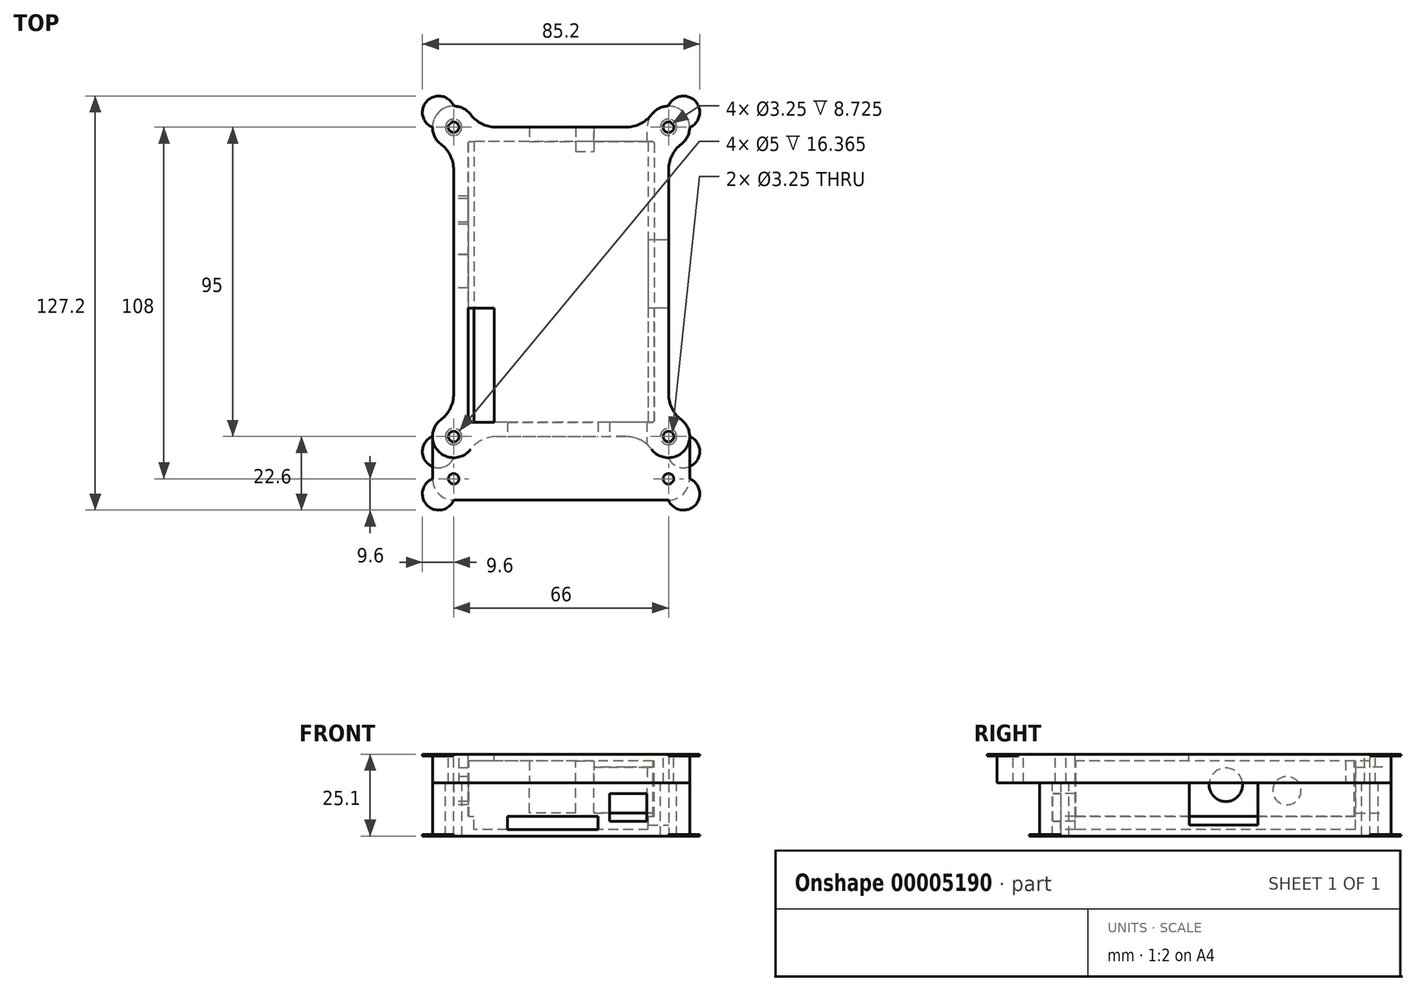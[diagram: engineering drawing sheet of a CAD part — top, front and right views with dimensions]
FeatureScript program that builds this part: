
annotation { "Feature Type Name" : "Feature", "Feature Type Description" : "" }
export const myFeature = defineFeature(function(context is Context, id is Id, definition is map)
    precondition{}
    {
        {
            var Q0;
            Q0=qCreatedBy(makeId("Top.planeOp"),FACE);
            var sketch = newSketch(context, id + "F0", { "sketchPlane" : qUnion([Q0])});
            skLineSegment(sketch, "E0.rect.bottom", {"start": v(28, 42.5) * mm, "end": v(-28, 42.5) * mm, "construction": true});
            skLineSegment(sketch, "E0.rect.top", {"start": v(28, -42.5) * mm, "end": v(-28, -42.5) * mm, "construction": true});
            skLineSegment(sketch, "E0.rect.left", {"start": v(28, 42.5) * mm, "end": v(28, -42.5) * mm, "construction": true});
            skLineSegment(sketch, "E0.rect.right", {"start": v(-28, 42.5) * mm, "end": v(-28, -42.5) * mm, "construction": true});
            skPoint(sketch, "E0.rect.middle", {"position": v(0, 0) * mm});
            skLineSegment(sketch, "E1.0", {"start": v(33, 47.5) * mm, "end": v(-33, 47.5) * mm});
            skLineSegment(sketch, "E1.1", {"start": v(33, 47.5) * mm, "end": v(33, -47.5) * mm});
            skLineSegment(sketch, "E1.2", {"start": v(33, -47.5) * mm, "end": v(-33, -47.5) * mm});
            skLineSegment(sketch, "E1.3", {"start": v(-33, 47.5) * mm, "end": v(-33, -47.5) * mm});
            skSolve(sketch);
        }
        {
            var Q0;
            Q0 = qSketchRegion(id + "F0", true);
            extrude(context, id + "F1", {"entities" : qUnion([Q0]), "depth" : (2 + 1.6 + 15.5 + 4) * mm});
        }
        {
            var Q0;
            Q0=makeQuery(id+"F1.opExtrude","CAP_FACE",FACE,{"disambiguationData":[OSD([sQuery(id+"F0.wireOp",EDGE,"E1.0"),sQuery(id+"F0.wireOp",EDGE,"E1.1"),sQuery(id+"F0.wireOp",EDGE,"E1.2"),sQuery(id+"F0.wireOp",EDGE,"E1.3")])],"isStart":false});
            var sketch = newSketch(context, id + "F2", { "sketchPlane" : qUnion([Q0])});
            skLineSegment(sketch, "E2.rect.bottom", {"start": v(28, 42.5) * mm, "end": v(-28, 42.5) * mm});
            skLineSegment(sketch, "E2.rect.top", {"start": v(28, -42.5) * mm, "end": v(-28, -42.5) * mm});
            skLineSegment(sketch, "E2.rect.left", {"start": v(28, 42.5) * mm, "end": v(28, -42.5) * mm});
            skLineSegment(sketch, "E2.rect.right", {"start": v(-28, 42.5) * mm, "end": v(-28, -42.5) * mm});
            skPoint(sketch, "E2.rect.middle", {"position": v(0, 0) * mm});
            skSolve(sketch);
        }
        {
            var Q0;
            Q0 = qSketchRegion(id + "F2", true);
            extrude(context, id + "F3", {"entities" : qUnion([Q0]), "operationType" : NewBodyOperationType.REMOVE, "oppositeDirection" : true, "depth" : (15.5 + 1.6) * mm});
        }
        {
            var Q0;
            Q0=makeQuery(id+"F3.boolean.opBoolean","COPY",FACE,{"derivedFrom":makeQuery(id+"F3.opExtrude","CAP_FACE",FACE,{"disambiguationData":[OSD([sQuery(id+"F2.wireOp",EDGE,"E2.rect.bottom"),sQuery(id+"F2.wireOp",EDGE,"E2.rect.top"),sQuery(id+"F2.wireOp",EDGE,"E2.rect.left"),sQuery(id+"F2.wireOp",EDGE,"E2.rect.right")])],"isStart":false})});
            var sketch = newSketch(context, id + "F4", { "sketchPlane" : qUnion([Q0])});
            skLineSegment(sketch, "E3.rect.bottom", {"start": v(26.75, 42.5) * mm, "end": v(-26.75, 42.5) * mm});
            skLineSegment(sketch, "E3.rect.top", {"start": v(26.75, -42.5) * mm, "end": v(-26.75, -42.5) * mm});
            skLineSegment(sketch, "E3.rect.left", {"start": v(26.75, 42.5) * mm, "end": v(26.75, -42.5) * mm});
            skLineSegment(sketch, "E3.rect.right", {"start": v(-26.75, 42.5) * mm, "end": v(-26.75, -42.5) * mm});
            skPoint(sketch, "E3.rect.middle", {"position": v(0, 0) * mm});
            skSolve(sketch);
        }
        {
            var Q0;
            Q0 = qSketchRegion(id + "F4", true);
            extrude(context, id + "F5", {"entities" : qUnion([Q0]), "operationType" : NewBodyOperationType.REMOVE, "oppositeDirection" : true, "depth" : 4 * mm});
        }
        {
            var Q0;
            Q0=makeQuery(id+"F1.opExtrude","SWEPT_FACE",FACE,{"disambiguationData":[OSD([sQuery(id+"F0.wireOp",EDGE,"E1.2")])]});
            var sketch = newSketch(context, id + "F6", { "sketchPlane" : qUnion([Q0])});
            skLineSegment(sketch, "E4.0", {"start": v(26.75, 2) * mm, "end": v(-26.75, 2) * mm, "construction": true});
            skLineSegment(sketch, "E4.1", {"start": v(-26.75, 6) * mm, "end": v(-28, 6) * mm, "construction": true});
            skLineSegment(sketch, "E5.bottom", {"start": v(-16.5, 2) * mm, "end": v(11.3, 2) * mm});
            skLineSegment(sketch, "E5.top", {"start": v(-16.5, 6) * mm, "end": v(11.3, 6) * mm});
            skLineSegment(sketch, "E5.left", {"start": v(-16.5, 2) * mm, "end": v(-16.5, 6) * mm});
            skLineSegment(sketch, "E5.right", {"start": v(11.3, 2) * mm, "end": v(11.3, 6) * mm});
            skLineSegment(sketch, "E6.0", {"start": v(28, 6) * mm, "end": v(26.75, 6) * mm, "construction": true});
            skLineSegment(sketch, "E7.bottom", {"start": v(24.4, 7.6) * mm, "end": v(16.8, 7.6) * mm, "construction": true});
            skLineSegment(sketch, "E7.top", {"start": v(24.4, 10) * mm, "end": v(16.8, 10) * mm, "construction": true});
            skLineSegment(sketch, "E7.left", {"start": v(24.4, 7.6) * mm, "end": v(24.4, 10) * mm, "construction": true});
            skLineSegment(sketch, "E7.right", {"start": v(16.8, 7.6) * mm, "end": v(16.8, 10) * mm, "construction": true});
            skLineSegment(sketch, "E8", {"start": v(20.6, 10) * mm, "end": v(20.6, 7.6) * mm, "construction": true});
            skPoint(sketch, "E9", {"position": v(20.6, 8.8) * mm});
            skLineSegment(sketch, "E10.rect.bottom", {"start": v(26.35, 13.05) * mm, "end": v(14.85, 13.05) * mm});
            skLineSegment(sketch, "E10.rect.top", {"start": v(26.35, 4.55) * mm, "end": v(14.85, 4.55) * mm});
            skLineSegment(sketch, "E10.rect.left", {"start": v(26.35, 13.05) * mm, "end": v(26.35, 4.55) * mm});
            skLineSegment(sketch, "E10.rect.right", {"start": v(14.85, 13.05) * mm, "end": v(14.85, 4.55) * mm});
            skSolve(sketch);
        }
        {
            var Q0;
            Q0 = qSketchRegion(id + "F6", true);
            var Q1;
            Q1=makeQuery(id+"F5.boolean.opBoolean","MERGE",FACE,{"derivedFrom":[makeQuery(id+"F3.boolean.opBoolean","COPY",FACE,{"derivedFrom":makeQuery(id+"F3.opExtrude","SWEPT_FACE",FACE,{"disambiguationData":[OSD([sQuery(id+"F2.wireOp",EDGE,"E2.rect.top")])]})}),makeQuery(id+"F5.opExtrude","SWEPT_FACE",FACE,{"disambiguationData":[OSD([sQuery(id+"F4.wireOp",EDGE,"E3.rect.top")])]})]});
            extrude(context, id + "F7", {"entities" : qUnion([Q0]), "operationType" : NewBodyOperationType.REMOVE, "endBound" : BoundingType.UP_TO_SURFACE, "oppositeDirection" : true, "endBoundEntityFace" : qUnion([Q1]), "depth" : 25 * mm});
        }
        {
            var Q0;
            Q0=makeQuery(id+"F1.opExtrude","SWEPT_FACE",FACE,{"disambiguationData":[OSD([sQuery(id+"F0.wireOp",EDGE,"E1.0")])]});
            var sketch = newSketch(context, id + "F8", { "sketchPlane" : qUnion([Q0])});
            skLineSegment(sketch, "E11.0", {"start": v(-28, 6) * mm, "end": v(-26.75, 6) * mm, "construction": true});
            skLineSegment(sketch, "E11.1", {"start": v(-26.75, 2) * mm, "end": v(26.75, 2) * mm, "construction": true});
            skLineSegment(sketch, "E11.2", {"start": v(26.75, 6) * mm, "end": v(28, 6) * mm, "construction": true});
            skLineSegment(sketch, "E12.bottom", {"start": v(-26, 7.6) * mm, "end": v(-10.6, 7.6) * mm, "construction": true});
            skLineSegment(sketch, "E12.top", {"start": v(-26, 20.6) * mm, "end": v(-10.6, 20.6) * mm, "construction": true});
            skLineSegment(sketch, "E12.left", {"start": v(-26, 7.6) * mm, "end": v(-26, 20.6) * mm, "construction": true});
            skLineSegment(sketch, "E12.right", {"start": v(-10.6, 7.6) * mm, "end": v(-10.6, 20.6) * mm, "construction": true});
            skLineSegment(sketch, "E13.bottom", {"start": v(-4.05, 7.6) * mm, "end": v(9.2, 7.6) * mm, "construction": true});
            skLineSegment(sketch, "E13.top", {"start": v(-4.05, 23.1) * mm, "end": v(9.2, 23.1) * mm, "construction": true});
            skLineSegment(sketch, "E13.left", {"start": v(-4.05, 7.6) * mm, "end": v(-4.05, 23.1) * mm, "construction": true});
            skLineSegment(sketch, "E13.right", {"start": v(9.2, 7.6) * mm, "end": v(9.2, 23.1) * mm, "construction": true});
            skLineSegment(sketch, "E14.0", {"start": v(-26.5, 21.1) * mm, "end": v(-10.1, 21.1) * mm});
            skLineSegment(sketch, "E14.1", {"start": v(-26.5, 7.1) * mm, "end": v(-26.5, 21.1) * mm});
            skLineSegment(sketch, "E14.2", {"start": v(-26.5, 7.1) * mm, "end": v(-10.1, 7.1) * mm});
            skLineSegment(sketch, "E14.3", {"start": v(-10.1, 7.1) * mm, "end": v(-10.1, 21.1) * mm});
            skLineSegment(sketch, "E15.0", {"start": v(-4.55, 23.6) * mm, "end": v(9.7, 23.6) * mm});
            skLineSegment(sketch, "E15.1", {"start": v(-4.55, 7.1) * mm, "end": v(-4.55, 23.6) * mm});
            skLineSegment(sketch, "E15.2", {"start": v(-4.55, 7.1) * mm, "end": v(9.7, 7.1) * mm});
            skLineSegment(sketch, "E15.3", {"start": v(9.7, 7.1) * mm, "end": v(9.7, 23.6) * mm});
            skSolve(sketch);
        }
        {
            var Q0;
            Q0 = qSketchRegion(id + "F8", true);
            var Q1;
            Q1=makeQuery(id+"F5.boolean.opBoolean","MERGE",FACE,{"derivedFrom":[makeQuery(id+"F3.boolean.opBoolean","COPY",FACE,{"derivedFrom":makeQuery(id+"F3.opExtrude","SWEPT_FACE",FACE,{"disambiguationData":[OSD([sQuery(id+"F2.wireOp",EDGE,"E2.rect.bottom")])]})}),makeQuery(id+"F5.opExtrude","SWEPT_FACE",FACE,{"disambiguationData":[OSD([sQuery(id+"F4.wireOp",EDGE,"E3.rect.bottom")])]})]});
            extrude(context, id + "F9", {"entities" : qUnion([Q0]), "operationType" : NewBodyOperationType.REMOVE, "endBound" : BoundingType.UP_TO_SURFACE, "oppositeDirection" : true, "endBoundEntityFace" : qUnion([Q1]), "depth" : 25 * mm});
        }
        {
            var Q0;
            Q0=makeQuery(id+"F1.opExtrude","SWEPT_FACE",FACE,{"disambiguationData":[OSD([sQuery(id+"F0.wireOp",EDGE,"E1.1")])]});
            var sketch = newSketch(context, id + "F10", { "sketchPlane" : qUnion([Q0])});
            skLineSegment(sketch, "E16.0", {"start": v(42.5, 6) * mm, "end": v(-42.5, 6) * mm, "construction": true});
            skLineSegment(sketch, "E17.bottom", {"start": v(-5, 6.8) * mm, "end": v(10.1, 6.8) * mm, "construction": true});
            skLineSegment(sketch, "E17.top", {"start": v(-5, 12.95) * mm, "end": v(10.1, 12.95) * mm, "construction": true});
            skLineSegment(sketch, "E17.left", {"start": v(-5, 6.8) * mm, "end": v(-5, 12.95) * mm, "construction": true});
            skLineSegment(sketch, "E17.right", {"start": v(10.1, 6.8) * mm, "end": v(10.1, 12.95) * mm, "construction": true});
            skLineSegment(sketch, "E18", {"start": v(2.55, 12.95) * mm, "end": v(2.55, 6.8) * mm, "construction": true});
            skPoint(sketch, "E19", {"position": v(2.55, 9.88) * mm});
            skLineSegment(sketch, "E20.rect.bottom", {"start": v(13.05, 16.38) * mm, "end": v(-7.95, 16.38) * mm});
            skLineSegment(sketch, "E20.rect.top", {"start": v(13.05, 3.38) * mm, "end": v(-7.95, 3.38) * mm});
            skLineSegment(sketch, "E20.rect.left", {"start": v(13.05, 16.38) * mm, "end": v(13.05, 3.38) * mm});
            skLineSegment(sketch, "E20.rect.right", {"start": v(-7.95, 16.38) * mm, "end": v(-7.95, 3.38) * mm});
            skSolve(sketch);
        }
        {
            var Q0;
            Q0 = qSketchRegion(id + "F10", true);
            var Q1;
            Q1=makeQuery(id+"F5.boolean.opBoolean","COPY",FACE,{"derivedFrom":makeQuery(id+"F5.opExtrude","SWEPT_FACE",FACE,{"disambiguationData":[OSD([sQuery(id+"F4.wireOp",EDGE,"E3.rect.left")])]})});
            extrude(context, id + "F11", {"entities" : qUnion([Q0]), "operationType" : NewBodyOperationType.REMOVE, "endBound" : BoundingType.UP_TO_SURFACE, "oppositeDirection" : true, "endBoundEntityFace" : qUnion([Q1]), "depth" : 25 * mm});
        }
        {
            var Q0;
            Q0=makeQuery(id+"F1.opExtrude","SWEPT_FACE",FACE,{"disambiguationData":[OSD([sQuery(id+"F0.wireOp",EDGE,"E1.3")])]});
            var sketch = newSketch(context, id + "F12", { "sketchPlane" : qUnion([Q0])});
            skLineSegment(sketch, "E21.0", {"start": v(-42.5, 6) * mm, "end": v(42.5, 6) * mm, "construction": true});
            skCircle(sketch, "E22", {"center": v(-22, 13.95) * mm, "radius": 3.35 * mm, "construction": true});
            skCircle(sketch, "E23", {"center": v(-3.25, 15.75) * mm, "radius": 4.15 * mm, "construction": true});
            skPoint(sketch, "E24", {"position": v(-22, 10.6) * mm});
            skPoint(sketch, "E25", {"position": v(-3.25, 11.6) * mm});
            skCircle(sketch, "E26.0", {"center": v(-22, 13.95) * mm, "radius": 4.35 * mm});
            skCircle(sketch, "E27.0", {"center": v(-3.25, 15.75) * mm, "radius": 5.15 * mm});
            skSolve(sketch);
        }
        {
            var Q0;
            Q0 = qSketchRegion(id + "F12", true);
            var Q1;
            Q1=makeQuery(id+"F3.boolean.opBoolean","COPY",FACE,{"derivedFrom":makeQuery(id+"F3.opExtrude","SWEPT_FACE",FACE,{"disambiguationData":[OSD([sQuery(id+"F2.wireOp",EDGE,"E2.rect.right")])]})});
            extrude(context, id + "F13", {"entities" : qUnion([Q0]), "operationType" : NewBodyOperationType.REMOVE, "endBound" : BoundingType.UP_TO_SURFACE, "oppositeDirection" : true, "endBoundEntityFace" : qUnion([Q1]), "depth" : 25 * mm});
        }
        {
            var Q0;
            Q0=makeQuery(id+"F1.opExtrude","CAP_FACE",FACE,{"disambiguationData":[OSD([sQuery(id+"F0.wireOp",EDGE,"E1.0"),sQuery(id+"F0.wireOp",EDGE,"E1.1"),sQuery(id+"F0.wireOp",EDGE,"E1.2"),sQuery(id+"F0.wireOp",EDGE,"E1.3")])],"isStart":false});
            var sketch = newSketch(context, id + "F14", { "sketchPlane" : qUnion([Q0])});
            skLineSegment(sketch, "E28.rect.bottom", {"start": v(28.58, 43.08) * mm, "end": v(-28.57, 43.08) * mm});
            skLineSegment(sketch, "E28.rect.top", {"start": v(28.57, -43.07) * mm, "end": v(-28.58, -43.07) * mm});
            skLineSegment(sketch, "E28.rect.left", {"start": v(28.58, 43.08) * mm, "end": v(28.57, -43.07) * mm});
            skLineSegment(sketch, "E28.rect.right", {"start": v(-28.57, 43.08) * mm, "end": v(-28.58, -43.07) * mm});
            skPoint(sketch, "E28.rect.middle", {"position": v(0, 0) * mm});
            skSolve(sketch);
        }
        {
            var Q0;
            Q0 = qSketchRegion(id + "F14", true);
            var Q1;
            {var subQ0=sQuery(id+"F2.wireOp",EDGE,"E2.rect.bottom");var subQ1=sQuery(id+"F2.wireOp",EDGE,"E2.rect.top");var subQ2=sQuery(id+"F2.wireOp",EDGE,"E2.rect.right");Q1=makeQuery(id+"F5.boolean.opBoolean","SPLIT",FACE,{"disambiguationData":[TD([makeQuery(id+"F3.boolean.opBoolean","COPY",FACE,{"derivedFrom":makeQuery(id+"F3.opExtrude","SWEPT_FACE",FACE,{"disambiguationData":[OSD([subQ2])]})})])],"derivedFrom":makeQuery(id+"F3.boolean.opBoolean","COPY",FACE,{"derivedFrom":makeQuery(id+"F3.opExtrude","CAP_FACE",FACE,{"disambiguationData":[OSD([subQ0,subQ1,sQuery(id+"F2.wireOp",EDGE,"E2.rect.left"),subQ2])],"isStart":false})})});}
            extrude(context, id + "F15", {"entities" : qUnion([Q0]), "operationType" : NewBodyOperationType.REMOVE, "endBound" : BoundingType.UP_TO_SURFACE, "oppositeDirection" : true, "endBoundEntityFace" : qUnion([Q1]), "depth" : 25 * mm});
        }
        {
            var Q0;
            {var subQ0=sQuery(id+"F2.wireOp",EDGE,"E2.rect.bottom");var subQ1=sQuery(id+"F2.wireOp",EDGE,"E2.rect.top");var subQ2=sQuery(id+"F2.wireOp",EDGE,"E2.rect.left");var subQ3=sQuery(id+"F2.wireOp",EDGE,"E2.rect.right");var subQ4=makeQuery(id+"F3.boolean.opBoolean","COPY",FACE,{"derivedFrom":makeQuery(id+"F3.opExtrude","CAP_FACE",FACE,{"disambiguationData":[OSD([subQ0,subQ1,subQ2,subQ3])],"isStart":false})});var subQ8=makeQuery(id+"F3.boolean.opBoolean","COPY",FACE,{"derivedFrom":makeQuery(id+"F3.opExtrude","SWEPT_FACE",FACE,{"disambiguationData":[OSD([subQ0])]})});var subQ10=makeQuery(id+"F3.boolean.opBoolean","COPY",FACE,{"derivedFrom":makeQuery(id+"F3.opExtrude","SWEPT_FACE",FACE,{"disambiguationData":[OSD([subQ2])]})});Q0=makeQuery(id+"F15.boolean.opBoolean","MERGE",FACE,{"derivedFrom":[makeQuery(id+"F5.boolean.opBoolean","SPLIT",FACE,{"disambiguationData":[TD([makeQuery(id+"F3.boolean.opBoolean","COPY",FACE,{"derivedFrom":makeQuery(id+"F3.opExtrude","SWEPT_FACE",FACE,{"disambiguationData":[OSD([subQ3])]})})])],"derivedFrom":subQ4}),makeQuery(id+"F11.boolean.opBoolean","SPLIT",FACE,{"disambiguationData":[TD([subQ8])],"derivedFrom":makeQuery(id+"F5.boolean.opBoolean","SPLIT",FACE,{"disambiguationData":[TD([subQ10])],"derivedFrom":subQ4})}),makeQuery(id+"F15.opExtrude","CAP_FACE",FACE,{"disambiguationData":[OSD([sQuery(id+"F14.wireOp",EDGE,"E28.rect.bottom"),sQuery(id+"F14.wireOp",EDGE,"E28.rect.top"),sQuery(id+"F14.wireOp",EDGE,"E28.rect.left"),sQuery(id+"F14.wireOp",EDGE,"E28.rect.right")])],"isStart":false})]});}
            var sketch = newSketch(context, id + "F16", { "sketchPlane" : qUnion([Q0])});
            skLineSegment(sketch, "E29.bottom", {"start": v(-26.75, 42.5) * mm, "end": v(26.75, 42.5) * mm});
            skLineSegment(sketch, "E29.top", {"start": v(-26.75, 43.08) * mm, "end": v(26.75, 43.08) * mm});
            skLineSegment(sketch, "E29.left", {"start": v(-26.75, 42.5) * mm, "end": v(-26.75, 43.08) * mm});
            skLineSegment(sketch, "E29.right", {"start": v(26.75, 42.5) * mm, "end": v(26.75, 43.08) * mm});
            skLineSegment(sketch, "E30.bottom", {"start": v(-26.75, -42.5) * mm, "end": v(26.75, -42.5) * mm});
            skLineSegment(sketch, "E30.top", {"start": v(-26.75, -43.07) * mm, "end": v(26.75, -43.07) * mm});
            skLineSegment(sketch, "E30.left", {"start": v(-26.75, -42.5) * mm, "end": v(-26.75, -43.07) * mm});
            skLineSegment(sketch, "E30.right", {"start": v(26.75, -42.5) * mm, "end": v(26.75, -43.07) * mm});
            skSolve(sketch);
        }
        {
            var Q0;
            Q0 = qSketchRegion(id + "F16", true);
            var Q1;
            Q1=makeQuery(id+"F7.boolean.opBoolean","MERGE",FACE,{"derivedFrom":[makeQuery(id+"F5.boolean.opBoolean","COPY",FACE,{"derivedFrom":makeQuery(id+"F5.opExtrude","CAP_FACE",FACE,{"disambiguationData":[OSD([sQuery(id+"F4.wireOp",EDGE,"E3.rect.bottom"),sQuery(id+"F4.wireOp",EDGE,"E3.rect.top"),sQuery(id+"F4.wireOp",EDGE,"E3.rect.left"),sQuery(id+"F4.wireOp",EDGE,"E3.rect.right")])],"isStart":false})}),makeQuery(id+"F7.opExtrude","SWEPT_FACE",FACE,{"disambiguationData":[OSD([sQuery(id+"F6.wireOp",EDGE,"E5.bottom")])]})]});
            extrude(context, id + "F17", {"entities" : qUnion([Q0]), "operationType" : NewBodyOperationType.REMOVE, "endBound" : BoundingType.UP_TO_SURFACE, "oppositeDirection" : true, "endBoundEntityFace" : qUnion([Q1]), "depth" : 25 * mm});
        }
        {
            var Q0;
            Q0=makeQuery(id+"F1.opExtrude","CAP_FACE",FACE,{"disambiguationData":[OSD([sQuery(id+"F0.wireOp",EDGE,"E1.0"),sQuery(id+"F0.wireOp",EDGE,"E1.1"),sQuery(id+"F0.wireOp",EDGE,"E1.2"),sQuery(id+"F0.wireOp",EDGE,"E1.3")])],"isStart":false});
            var sketch = newSketch(context, id + "F18", { "sketchPlane" : qUnion([Q0])});
            skLineSegment(sketch, "E31.bottom", {"start": v(-33, 47.5) * mm, "end": v(33, 47.5) * mm});
            skLineSegment(sketch, "E31.top", {"start": v(-33, -47.5) * mm, "end": v(33, -47.5) * mm});
            skLineSegment(sketch, "E31.left", {"start": v(-33, 47.5) * mm, "end": v(-33, -47.5) * mm});
            skLineSegment(sketch, "E31.right", {"start": v(33, 47.5) * mm, "end": v(33, -47.5) * mm});
            skSolve(sketch);
        }
        {
            var Q0;
            Q0 = qSketchRegion(id + "F18", true);
            extrude(context, id + "F19", {"entities" : qUnion([Q0]), "operationType" : NewBodyOperationType.ADD, "depth" : 2 * mm});
        }
        {
            var Q0;
            Q0=makeQuery(id+"F19.opExtrude","CAP_FACE",FACE,{"disambiguationData":[OSD([sQuery(id+"F18.wireOp",EDGE,"E31.bottom"),sQuery(id+"F18.wireOp",EDGE,"E31.top"),sQuery(id+"F18.wireOp",EDGE,"E31.left"),sQuery(id+"F18.wireOp",EDGE,"E31.right")])],"isStart":false});
            var sketch = newSketch(context, id + "F20", { "sketchPlane" : qUnion([Q0])});
            skCircle(sketch, "E32", {"center": v(-33, 47.5) * mm, "radius": 6.5 * mm});
            skCircle(sketch, "E33", {"center": v(33, 47.5) * mm, "radius": 6.5 * mm});
            skCircle(sketch, "E34", {"center": v(33, -47.5) * mm, "radius": 6.5 * mm});
            skCircle(sketch, "E35", {"center": v(-33, -47.5) * mm, "radius": 6.5 * mm});
            skSolve(sketch);
        }
        {
            var Q0;
            Q0 = qSketchRegion(id + "F20", true);
            var Q1;
            Q1=makeQuery(id+"F1.opExtrude","CAP_FACE",FACE,{"disambiguationData":[OSD([sQuery(id+"F0.wireOp",EDGE,"E1.0"),sQuery(id+"F0.wireOp",EDGE,"E1.1"),sQuery(id+"F0.wireOp",EDGE,"E1.2"),sQuery(id+"F0.wireOp",EDGE,"E1.3")])],"isStart":true});
            extrude(context, id + "F21", {"entities" : qUnion([Q0]), "operationType" : NewBodyOperationType.ADD, "endBound" : BoundingType.UP_TO_SURFACE, "oppositeDirection" : true, "endBoundEntityFace" : qUnion([Q1]), "depth" : 25 * mm});
        }
        {
            var Q0;
            Q0=makeQuery(id+"F21.boolean.opBoolean","MERGE",FACE,{"derivedFrom":[makeQuery(id+"F19.opExtrude","CAP_FACE",FACE,{"disambiguationData":[OSD([sQuery(id+"F18.wireOp",EDGE,"E31.bottom"),sQuery(id+"F18.wireOp",EDGE,"E31.top"),sQuery(id+"F18.wireOp",EDGE,"E31.left"),sQuery(id+"F18.wireOp",EDGE,"E31.right")])],"isStart":false}),makeQuery(id+"F21.opExtrude","CAP_FACE",FACE,{"disambiguationData":[OSD([sQuery(id+"F20.wireOp",EDGE,"E32")])],"isStart":true}),makeQuery(id+"F21.opExtrude","CAP_FACE",FACE,{"disambiguationData":[OSD([sQuery(id+"F20.wireOp",EDGE,"E33")])],"isStart":true}),makeQuery(id+"F21.opExtrude","CAP_FACE",FACE,{"disambiguationData":[OSD([sQuery(id+"F20.wireOp",EDGE,"E34")])],"isStart":true}),makeQuery(id+"F21.opExtrude","CAP_FACE",FACE,{"disambiguationData":[OSD([sQuery(id+"F20.wireOp",EDGE,"E35")])],"isStart":true})]});
            var sketch = newSketch(context, id + "F22", { "sketchPlane" : qUnion([Q0])});
            skCircle(sketch, "E36", {"center": v(-33, -47.5) * mm, "radius": 1.63 * mm});
            skCircle(sketch, "E37", {"center": v(33, -47.5) * mm, "radius": 1.63 * mm});
            skCircle(sketch, "E38", {"center": v(33, 47.5) * mm, "radius": 1.63 * mm});
            skCircle(sketch, "E39", {"center": v(-33, 47.5) * mm, "radius": 1.63 * mm});
            skSolve(sketch);
        }
        {
            var Q0;
            Q0 = qSketchRegion(id + "F22", true);
            extrude(context, id + "F23", {"entities" : qUnion([Q0]), "operationType" : NewBodyOperationType.REMOVE, "endBound" : BoundingType.THROUGH_ALL, "oppositeDirection" : true, "depth" : 25 * mm});
        }
        {
            var Q0;
            Q0=makeQuery(id+"F21.boolean.opBoolean","INTERSECT",EDGE,{"derivedFrom":[makeQuery(id+"F19.boolean.opBoolean","MERGE",FACE,{"derivedFrom":[makeQuery(id+"F1.opExtrude","SWEPT_FACE",FACE,{"disambiguationData":[OSD([sQuery(id+"F0.wireOp",EDGE,"E1.3")])]}),makeQuery(id+"F19.opExtrude","SWEPT_FACE",FACE,{"disambiguationData":[OSD([sQuery(id+"F18.wireOp",EDGE,"E31.left")])]})]}),makeQuery(id+"F21.opExtrude","SWEPT_FACE",FACE,{"disambiguationData":[OSD([sQuery(id+"F20.wireOp",EDGE,"E32")])]})]});
            var Q1;
            Q1=makeQuery(id+"F21.boolean.opBoolean","INTERSECT",EDGE,{"derivedFrom":[makeQuery(id+"F19.boolean.opBoolean","MERGE",FACE,{"derivedFrom":[makeQuery(id+"F1.opExtrude","SWEPT_FACE",FACE,{"disambiguationData":[OSD([sQuery(id+"F0.wireOp",EDGE,"E1.3")])]}),makeQuery(id+"F19.opExtrude","SWEPT_FACE",FACE,{"disambiguationData":[OSD([sQuery(id+"F18.wireOp",EDGE,"E31.left")])]})]}),makeQuery(id+"F21.opExtrude","SWEPT_FACE",FACE,{"disambiguationData":[OSD([sQuery(id+"F20.wireOp",EDGE,"E35")])]})]});
            var Q2;
            Q2=makeQuery(id+"F21.boolean.opBoolean","INTERSECT",EDGE,{"derivedFrom":[makeQuery(id+"F19.boolean.opBoolean","MERGE",FACE,{"derivedFrom":[makeQuery(id+"F1.opExtrude","SWEPT_FACE",FACE,{"disambiguationData":[OSD([sQuery(id+"F0.wireOp",EDGE,"E1.2")])]}),makeQuery(id+"F19.opExtrude","SWEPT_FACE",FACE,{"disambiguationData":[OSD([sQuery(id+"F18.wireOp",EDGE,"E31.top")])]})]}),makeQuery(id+"F21.opExtrude","SWEPT_FACE",FACE,{"disambiguationData":[OSD([sQuery(id+"F20.wireOp",EDGE,"E35")])]})]});
            var Q3;
            Q3=makeQuery(id+"F21.boolean.opBoolean","INTERSECT",EDGE,{"derivedFrom":[makeQuery(id+"F19.boolean.opBoolean","MERGE",FACE,{"derivedFrom":[makeQuery(id+"F1.opExtrude","SWEPT_FACE",FACE,{"disambiguationData":[OSD([sQuery(id+"F0.wireOp",EDGE,"E1.2")])]}),makeQuery(id+"F19.opExtrude","SWEPT_FACE",FACE,{"disambiguationData":[OSD([sQuery(id+"F18.wireOp",EDGE,"E31.top")])]})]}),makeQuery(id+"F21.opExtrude","SWEPT_FACE",FACE,{"disambiguationData":[OSD([sQuery(id+"F20.wireOp",EDGE,"E34")])]})]});
            var Q4;
            Q4=makeQuery(id+"F21.boolean.opBoolean","INTERSECT",EDGE,{"derivedFrom":[makeQuery(id+"F19.boolean.opBoolean","MERGE",FACE,{"derivedFrom":[makeQuery(id+"F1.opExtrude","SWEPT_FACE",FACE,{"disambiguationData":[OSD([sQuery(id+"F0.wireOp",EDGE,"E1.1")])]}),makeQuery(id+"F19.opExtrude","SWEPT_FACE",FACE,{"disambiguationData":[OSD([sQuery(id+"F18.wireOp",EDGE,"E31.right")])]})]}),makeQuery(id+"F21.opExtrude","SWEPT_FACE",FACE,{"disambiguationData":[OSD([sQuery(id+"F20.wireOp",EDGE,"E34")])]})]});
            var Q5;
            Q5=makeQuery(id+"F21.boolean.opBoolean","INTERSECT",EDGE,{"derivedFrom":[makeQuery(id+"F19.boolean.opBoolean","MERGE",FACE,{"derivedFrom":[makeQuery(id+"F1.opExtrude","SWEPT_FACE",FACE,{"disambiguationData":[OSD([sQuery(id+"F0.wireOp",EDGE,"E1.1")])]}),makeQuery(id+"F19.opExtrude","SWEPT_FACE",FACE,{"disambiguationData":[OSD([sQuery(id+"F18.wireOp",EDGE,"E31.right")])]})]}),makeQuery(id+"F21.opExtrude","SWEPT_FACE",FACE,{"disambiguationData":[OSD([sQuery(id+"F20.wireOp",EDGE,"E33")])]})]});
            var Q6;
            Q6=makeQuery(id+"F21.boolean.opBoolean","INTERSECT",EDGE,{"derivedFrom":[makeQuery(id+"F19.boolean.opBoolean","MERGE",FACE,{"derivedFrom":[makeQuery(id+"F1.opExtrude","SWEPT_FACE",FACE,{"disambiguationData":[OSD([sQuery(id+"F0.wireOp",EDGE,"E1.0")])]}),makeQuery(id+"F19.opExtrude","SWEPT_FACE",FACE,{"disambiguationData":[OSD([sQuery(id+"F18.wireOp",EDGE,"E31.bottom")])]})]}),makeQuery(id+"F21.opExtrude","SWEPT_FACE",FACE,{"disambiguationData":[OSD([sQuery(id+"F20.wireOp",EDGE,"E33")])]})]});
            var Q7;
            Q7=makeQuery(id+"F21.boolean.opBoolean","INTERSECT",EDGE,{"derivedFrom":[makeQuery(id+"F19.boolean.opBoolean","MERGE",FACE,{"derivedFrom":[makeQuery(id+"F1.opExtrude","SWEPT_FACE",FACE,{"disambiguationData":[OSD([sQuery(id+"F0.wireOp",EDGE,"E1.0")])]}),makeQuery(id+"F19.opExtrude","SWEPT_FACE",FACE,{"disambiguationData":[OSD([sQuery(id+"F18.wireOp",EDGE,"E31.bottom")])]})]}),makeQuery(id+"F21.opExtrude","SWEPT_FACE",FACE,{"disambiguationData":[OSD([sQuery(id+"F20.wireOp",EDGE,"E32")])]})]});
            fillet(context, id + "F24", {"entities" : qUnion([Q0, Q1, Q2, Q3, Q4, Q5, Q6, Q7]), "radius" : 10 * mm, "tangentPropagation" : true, "allowEdgeOverflow" : false});
        }
        {
            var Q0;
            Q0=makeQuery(id+"F19.boolean.opBoolean","MERGE",FACE,{"derivedFrom":[makeQuery(id+"F1.opExtrude","SWEPT_FACE",FACE,{"disambiguationData":[OSD([sQuery(id+"F0.wireOp",EDGE,"E1.1")])]}),makeQuery(id+"F19.opExtrude","SWEPT_FACE",FACE,{"disambiguationData":[OSD([sQuery(id+"F18.wireOp",EDGE,"E31.right")])]})]});
            var sketch = newSketch(context, id + "F25", { "sketchPlane" : qUnion([Q0])});
            skLineSegment(sketch, "E40.bottom", {"start": v(-61.72, 16.38) * mm, "end": v(58.28, 16.38) * mm});
            skLineSegment(sketch, "E40.top", {"start": v(-61.72, 16.37) * mm, "end": v(58.28, 16.37) * mm});
            skLineSegment(sketch, "E40.left", {"start": v(-61.72, 16.38) * mm, "end": v(-61.72, 16.37) * mm});
            skLineSegment(sketch, "E40.right", {"start": v(58.28, 16.38) * mm, "end": v(58.28, 16.37) * mm});
            skSolve(sketch);
        }
        {
            var Q0;
            Q0 = qSketchRegion(id + "F25", true);
            extrude(context, id + "F26", {"entities" : qUnion([Q0]), "operationType" : NewBodyOperationType.REMOVE, "endBound" : BoundingType.THROUGH_ALL, "oppositeDirection" : true, "depth" : 25 * mm, "hasSecondDirection" : true, "secondDirectionBound" : BoundingType.THROUGH_ALL, "secondDirectionOppositeDirection" : false, "secondDirectionDepth" : 25 * mm});
        }
        {
            var Q0;
            Q0=makeQuery(id+"F21.boolean.opBoolean","MERGE",FACE,{"derivedFrom":[makeQuery(id+"F19.opExtrude","CAP_FACE",FACE,{"disambiguationData":[OSD([sQuery(id+"F18.wireOp",EDGE,"E31.bottom"),sQuery(id+"F18.wireOp",EDGE,"E31.top"),sQuery(id+"F18.wireOp",EDGE,"E31.left"),sQuery(id+"F18.wireOp",EDGE,"E31.right")])],"isStart":false}),makeQuery(id+"F21.opExtrude","CAP_FACE",FACE,{"disambiguationData":[OSD([sQuery(id+"F20.wireOp",EDGE,"E32")])],"isStart":true}),makeQuery(id+"F21.opExtrude","CAP_FACE",FACE,{"disambiguationData":[OSD([sQuery(id+"F20.wireOp",EDGE,"E33")])],"isStart":true}),makeQuery(id+"F21.opExtrude","CAP_FACE",FACE,{"disambiguationData":[OSD([sQuery(id+"F20.wireOp",EDGE,"E34")])],"isStart":true}),makeQuery(id+"F21.opExtrude","CAP_FACE",FACE,{"disambiguationData":[OSD([sQuery(id+"F20.wireOp",EDGE,"E35")])],"isStart":true})]});
            var sketch = newSketch(context, id + "F27", { "sketchPlane" : qUnion([Q0])});
            skLineSegment(sketch, "E41.bottom", {"start": v(-28.58, -43.07) * mm, "end": v(-20.57, -43.07) * mm});
            skLineSegment(sketch, "E41.top", {"start": v(-28.58, -8.08) * mm, "end": v(-20.58, -8.08) * mm});
            skLineSegment(sketch, "E41.left", {"start": v(-28.57, -43.07) * mm, "end": v(-28.58, -8.07) * mm});
            skLineSegment(sketch, "E41.right", {"start": v(-20.57, -43.07) * mm, "end": v(-20.58, -8.07) * mm});
            skSolve(sketch);
        }
        {
            var Q0;
            Q0 = qSketchRegion(id + "F27", true);
            extrude(context, id + "F28", {"entities" : qUnion([Q0]), "operationType" : NewBodyOperationType.REMOVE, "endBound" : BoundingType.UP_TO_NEXT, "oppositeDirection" : true, "depth" : 3 * mm});
        }
        {
            var Q0;
            Q0=makeQuery(id+"F26.boolean.opBoolean","COPY",FACE,{"disambiguationData":[OD(1.0)],"derivedFrom":makeQuery(id+"F26.opExtrude","SWEPT_FACE",FACE,{"disambiguationData":[OSD([sQuery(id+"F25.wireOp",EDGE,"E40.top")])]})});
            var sketch = newSketch(context, id + "F29", { "sketchPlane" : qUnion([Q0])});
            skCircle(sketch, "E42", {"center": v(-33, 47.5) * mm, "radius": 2.5 * mm});
            skCircle(sketch, "E43", {"center": v(33, 47.5) * mm, "radius": 2.5 * mm});
            skCircle(sketch, "E44", {"center": v(-33, -47.5) * mm, "radius": 2.5 * mm});
            skCircle(sketch, "E45", {"center": v(33, -47.5) * mm, "radius": 2.5 * mm});
            skSolve(sketch);
        }
        {
            var Q0;
            Q0 = qSketchRegion(id + "F29", true);
            var Q1;
            Q1=makeQuery(id+"F17.boolean.opBoolean","MERGE",FACE,{"derivedFrom":[makeQuery(id+"F7.boolean.opBoolean","MERGE",FACE,{"derivedFrom":[makeQuery(id+"F5.boolean.opBoolean","COPY",FACE,{"derivedFrom":makeQuery(id+"F5.opExtrude","CAP_FACE",FACE,{"disambiguationData":[OSD([sQuery(id+"F4.wireOp",EDGE,"E3.rect.bottom"),sQuery(id+"F4.wireOp",EDGE,"E3.rect.top"),sQuery(id+"F4.wireOp",EDGE,"E3.rect.left"),sQuery(id+"F4.wireOp",EDGE,"E3.rect.right")])],"isStart":false})}),makeQuery(id+"F7.opExtrude","SWEPT_FACE",FACE,{"disambiguationData":[OSD([sQuery(id+"F6.wireOp",EDGE,"E5.bottom")])]})]}),makeQuery(id+"F17.opExtrude","CAP_FACE",FACE,{"disambiguationData":[OSD([sQuery(id+"F16.wireOp",EDGE,"E29.bottom"),sQuery(id+"F16.wireOp",EDGE,"E29.top"),sQuery(id+"F16.wireOp",EDGE,"E29.left"),sQuery(id+"F16.wireOp",EDGE,"E29.right")])],"isStart":false}),makeQuery(id+"F17.opExtrude","CAP_FACE",FACE,{"disambiguationData":[OSD([sQuery(id+"F16.wireOp",EDGE,"E30.bottom"),sQuery(id+"F16.wireOp",EDGE,"E30.top"),sQuery(id+"F16.wireOp",EDGE,"E30.left"),sQuery(id+"F16.wireOp",EDGE,"E30.right")])],"isStart":false})]});
            extrude(context, id + "F30", {"entities" : qUnion([Q0]), "operationType" : NewBodyOperationType.REMOVE, "endBound" : BoundingType.UP_TO_SURFACE, "oppositeDirection" : true, "endBoundEntityFace" : qUnion([Q1]), "depth" : 13 * mm});
        }
        {
            var Q0;
            Q0=makeQuery(id+"F21.boolean.opBoolean","MERGE",FACE,{"derivedFrom":[makeQuery(id+"F1.opExtrude","CAP_FACE",FACE,{"disambiguationData":[OSD([sQuery(id+"F0.wireOp",EDGE,"E1.0"),sQuery(id+"F0.wireOp",EDGE,"E1.1"),sQuery(id+"F0.wireOp",EDGE,"E1.2"),sQuery(id+"F0.wireOp",EDGE,"E1.3")])],"isStart":true}),makeQuery(id+"F21.opExtrude","CAP_FACE",FACE,{"disambiguationData":[OSD([sQuery(id+"F20.wireOp",EDGE,"E32")])],"isStart":false}),makeQuery(id+"F21.opExtrude","CAP_FACE",FACE,{"disambiguationData":[OSD([sQuery(id+"F20.wireOp",EDGE,"E33")])],"isStart":false}),makeQuery(id+"F21.opExtrude","CAP_FACE",FACE,{"disambiguationData":[OSD([sQuery(id+"F20.wireOp",EDGE,"E34")])],"isStart":false}),makeQuery(id+"F21.opExtrude","CAP_FACE",FACE,{"disambiguationData":[OSD([sQuery(id+"F20.wireOp",EDGE,"E35")])],"isStart":false})]});
            var sketch = newSketch(context, id + "F31", { "sketchPlane" : qUnion([Q0])});
            skCircle(sketch, "E46.0", {"center": v(-33, -47.5) * mm, "radius": 1.63 * mm});
            skCircle(sketch, "E46.1", {"center": v(-33, 47.5) * mm, "radius": 1.63 * mm});
            skCircle(sketch, "E46.2", {"center": v(33, 47.5) * mm, "radius": 1.63 * mm});
            skCircle(sketch, "E46.3", {"center": v(33, -47.5) * mm, "radius": 1.63 * mm});
            skSolve(sketch);
        }
        {
            var Q0;
            Q0 = qSketchRegion(id + "F31", true);
            var Q1;
            Q1=makeQuery(id+"F30.boolean.opBoolean","COPY",FACE,{"derivedFrom":makeQuery(id+"F30.opExtrude","CAP_FACE",FACE,{"disambiguationData":[OSD([sQuery(id+"F29.wireOp",EDGE,"E43")])],"isStart":false})});
            extrude(context, id + "F32", {"entities" : qUnion([Q0]), "operationType" : NewBodyOperationType.ADD, "endBound" : BoundingType.UP_TO_SURFACE, "oppositeDirection" : true, "endBoundEntityFace" : qUnion([Q1]), "depth" : 25 * mm});
        }
        {
            var Q0;
            Q0=makeQuery(id+"F26.boolean.opBoolean","COPY",FACE,{"disambiguationData":[OD(1.0)],"derivedFrom":makeQuery(id+"F26.opExtrude","SWEPT_FACE",FACE,{"disambiguationData":[OSD([sQuery(id+"F25.wireOp",EDGE,"E40.bottom")])]})});
            var sketch = newSketch(context, id + "F33", { "sketchPlane" : qUnion([Q0])});
            skLineSegment(sketch, "E47.bottom", {"start": v(4.55, -43.08) * mm, "end": v(10.1, -43.08) * mm});
            skLineSegment(sketch, "E47.top", {"start": v(4.55, -40.08) * mm, "end": v(10.1, -40.08) * mm});
            skLineSegment(sketch, "E47.left", {"start": v(4.55, -43.08) * mm, "end": v(4.55, -40.08) * mm});
            skLineSegment(sketch, "E47.right", {"start": v(10.1, -43.07) * mm, "end": v(10.1, -40.08) * mm});
            skSolve(sketch);
        }
        {
            var Q0;
            Q0 = qSketchRegion(id + "F33", true);
            var Q1;
            Q1=makeQuery(id+"F19.opExtrude","CAP_FACE",FACE,{"disambiguationData":[OSD([sQuery(id+"F18.wireOp",EDGE,"E31.bottom"),sQuery(id+"F18.wireOp",EDGE,"E31.top"),sQuery(id+"F18.wireOp",EDGE,"E31.left"),sQuery(id+"F18.wireOp",EDGE,"E31.right")])],"isStart":true});
            extrude(context, id + "F34", {"entities" : qUnion([Q0]), "operationType" : NewBodyOperationType.ADD, "endBound" : BoundingType.UP_TO_SURFACE, "oppositeDirection" : true, "endBoundEntityFace" : qUnion([Q1]), "depth" : 25 * mm});
        }
        {
            var Q0;
            Q0=makeQuery(id+"F32.boolean.opBoolean","MERGE",FACE,{"derivedFrom":[makeQuery(id+"F21.boolean.opBoolean","MERGE",FACE,{"derivedFrom":[makeQuery(id+"F1.opExtrude","CAP_FACE",FACE,{"disambiguationData":[OSD([sQuery(id+"F0.wireOp",EDGE,"E1.0"),sQuery(id+"F0.wireOp",EDGE,"E1.1"),sQuery(id+"F0.wireOp",EDGE,"E1.2"),sQuery(id+"F0.wireOp",EDGE,"E1.3")])],"isStart":true}),makeQuery(id+"F21.opExtrude","CAP_FACE",FACE,{"disambiguationData":[OSD([sQuery(id+"F20.wireOp",EDGE,"E32")])],"isStart":false}),makeQuery(id+"F21.opExtrude","CAP_FACE",FACE,{"disambiguationData":[OSD([sQuery(id+"F20.wireOp",EDGE,"E33")])],"isStart":false}),makeQuery(id+"F21.opExtrude","CAP_FACE",FACE,{"disambiguationData":[OSD([sQuery(id+"F20.wireOp",EDGE,"E34")])],"isStart":false}),makeQuery(id+"F21.opExtrude","CAP_FACE",FACE,{"disambiguationData":[OSD([sQuery(id+"F20.wireOp",EDGE,"E35")])],"isStart":false})]}),makeQuery(id+"F32.opExtrude","CAP_FACE",FACE,{"disambiguationData":[OSD([sQuery(id+"F31.wireOp",EDGE,"E46.0")])],"isStart":true}),makeQuery(id+"F32.opExtrude","CAP_FACE",FACE,{"disambiguationData":[OSD([sQuery(id+"F31.wireOp",EDGE,"E46.1")])],"isStart":true}),makeQuery(id+"F32.opExtrude","CAP_FACE",FACE,{"disambiguationData":[OSD([sQuery(id+"F31.wireOp",EDGE,"E46.2")])],"isStart":true}),makeQuery(id+"F32.opExtrude","CAP_FACE",FACE,{"disambiguationData":[OSD([sQuery(id+"F31.wireOp",EDGE,"E46.3")])],"isStart":true})]});
            var sketch = newSketch(context, id + "F35", { "sketchPlane" : qUnion([Q0])});
            skCircle(sketch, "E48.0", {"center": v(33, 47.5) * mm, "radius": 2.5 * mm});
            skCircle(sketch, "E48.1", {"center": v(-33, 47.5) * mm, "radius": 2.5 * mm});
            skCircle(sketch, "E49.0", {"center": v(33, -47.5) * mm, "radius": 2.5 * mm});
            skCircle(sketch, "E49.1", {"center": v(-33, -47.5) * mm, "radius": 2.5 * mm});
            skSolve(sketch);
        }
        {
            var Q0;
            Q0 = qSketchRegion(id + "F35", true);
            var Q1;
            Q1=makeQuery(id+"F26.boolean.opBoolean","COPY",FACE,{"disambiguationData":[OD(2.0)],"derivedFrom":makeQuery(id+"F26.opExtrude","SWEPT_FACE",FACE,{"disambiguationData":[OSD([sQuery(id+"F25.wireOp",EDGE,"E40.top")])]})});
            extrude(context, id + "F36", {"entities" : qUnion([Q0]), "operationType" : NewBodyOperationType.REMOVE, "endBound" : BoundingType.UP_TO_SURFACE, "oppositeDirection" : true, "endBoundEntityFace" : qUnion([Q1]), "depth" : 25 * mm});
        }
        {
            var Q0;
            Q0=makeQuery(id+"F32.boolean.opBoolean","MERGE",FACE,{"derivedFrom":[makeQuery(id+"F21.boolean.opBoolean","MERGE",FACE,{"derivedFrom":[makeQuery(id+"F1.opExtrude","CAP_FACE",FACE,{"disambiguationData":[OSD([sQuery(id+"F0.wireOp",EDGE,"E1.0"),sQuery(id+"F0.wireOp",EDGE,"E1.1"),sQuery(id+"F0.wireOp",EDGE,"E1.2"),sQuery(id+"F0.wireOp",EDGE,"E1.3")])],"isStart":true}),makeQuery(id+"F21.opExtrude","CAP_FACE",FACE,{"disambiguationData":[OSD([sQuery(id+"F20.wireOp",EDGE,"E32")])],"isStart":false}),makeQuery(id+"F21.opExtrude","CAP_FACE",FACE,{"disambiguationData":[OSD([sQuery(id+"F20.wireOp",EDGE,"E33")])],"isStart":false}),makeQuery(id+"F21.opExtrude","CAP_FACE",FACE,{"disambiguationData":[OSD([sQuery(id+"F20.wireOp",EDGE,"E34")])],"isStart":false}),makeQuery(id+"F21.opExtrude","CAP_FACE",FACE,{"disambiguationData":[OSD([sQuery(id+"F20.wireOp",EDGE,"E35")])],"isStart":false})]}),makeQuery(id+"F32.opExtrude","CAP_FACE",FACE,{"disambiguationData":[OSD([sQuery(id+"F31.wireOp",EDGE,"E46.0")])],"isStart":true}),makeQuery(id+"F32.opExtrude","CAP_FACE",FACE,{"disambiguationData":[OSD([sQuery(id+"F31.wireOp",EDGE,"E46.1")])],"isStart":true}),makeQuery(id+"F32.opExtrude","CAP_FACE",FACE,{"disambiguationData":[OSD([sQuery(id+"F31.wireOp",EDGE,"E46.2")])],"isStart":true}),makeQuery(id+"F32.opExtrude","CAP_FACE",FACE,{"disambiguationData":[OSD([sQuery(id+"F31.wireOp",EDGE,"E46.3")])],"isStart":true})]});
            var sketch = newSketch(context, id + "F37", { "sketchPlane" : qUnion([Q0])});
            skCircle(sketch, "E50", {"center": v(37.6, 52.1) * mm, "radius": 5 * mm});
            skCircle(sketch, "E51", {"center": v(37.6, -52.1) * mm, "radius": 5 * mm});
            skCircle(sketch, "E52", {"center": v(-37.6, -52.1) * mm, "radius": 5 * mm});
            skCircle(sketch, "E53", {"center": v(-37.6, 52.1) * mm, "radius": 5 * mm});
            skSolve(sketch);
        }
        {
            var Q0;
            Q0 = qSketchRegion(id + "F37", true);
            extrude(context, id + "F38", {"entities" : qUnion([Q0]), "operationType" : NewBodyOperationType.ADD, "oppositeDirection" : true, "depth" : 0.5 * mm});
        }
        {
            var Q0;
            Q0=makeQuery(id+"F21.boolean.opBoolean","MERGE",FACE,{"derivedFrom":[makeQuery(id+"F19.opExtrude","CAP_FACE",FACE,{"disambiguationData":[OSD([sQuery(id+"F18.wireOp",EDGE,"E31.bottom"),sQuery(id+"F18.wireOp",EDGE,"E31.top"),sQuery(id+"F18.wireOp",EDGE,"E31.left"),sQuery(id+"F18.wireOp",EDGE,"E31.right")])],"isStart":false}),makeQuery(id+"F21.opExtrude","CAP_FACE",FACE,{"disambiguationData":[OSD([sQuery(id+"F20.wireOp",EDGE,"E32")])],"isStart":true}),makeQuery(id+"F21.opExtrude","CAP_FACE",FACE,{"disambiguationData":[OSD([sQuery(id+"F20.wireOp",EDGE,"E33")])],"isStart":true}),makeQuery(id+"F21.opExtrude","CAP_FACE",FACE,{"disambiguationData":[OSD([sQuery(id+"F20.wireOp",EDGE,"E34")])],"isStart":true}),makeQuery(id+"F21.opExtrude","CAP_FACE",FACE,{"disambiguationData":[OSD([sQuery(id+"F20.wireOp",EDGE,"E35")])],"isStart":true})]});
            var sketch = newSketch(context, id + "F39", { "sketchPlane" : qUnion([Q0])});
            skLineSegment(sketch, "E54", {"start": v(0, -47.5) * mm, "end": v(0, 0) * mm, "construction": true});
            skLineSegment(sketch, "E55", {"start": v(-33, -47.5) * mm, "end": v(-33, -60.5) * mm, "construction": true});
            skCircle(sketch, "E56", {"center": v(-33, -60.5) * mm, "radius": 1.63 * mm});
            skArc(sketch, "E57.0", {"start": v(-39.5, -47.5) * mm, "mid": v(-35.08, -53.66) * mm, "end": v(-27.83, -51.44) * mm});
            skArc(sketch, "E57.1", {"start": v(-27.83, -51.44) * mm, "mid": v(-24.31, -48.54) * mm, "end": v(-19.88, -47.5) * mm});
            skArc(sketch, "E58", {"start": v(-39.5, -60.5) * mm, "mid": v(-37.6, -65.1) * mm, "end": v(-33, -67) * mm});
            skLineSegment(sketch, "E59", {"start": v(-39.5, -47.5) * mm, "end": v(-39.5, -60.5) * mm});
            skCircle(sketch, "E60", {"center": v(-33, -60.5) * mm, "radius": 6.5 * mm, "construction": true});
            skPoint(sketch, "E61.orphan", {"position": v(-36.94, -42.33) * mm});
            skLineSegment(sketch, "E62.MirrorCS", {"start": v(39.5, -47.5) * mm, "end": v(39.5, -60.5) * mm});
            skPoint(sketch, "E63.MirrorP", {"position": v(36.94, -42.33) * mm});
            skArc(sketch, "E64.MirrorCS", {"start": v(39.5, -47.5) * mm, "mid": v(35.08, -53.66) * mm, "end": v(27.83, -51.44) * mm});
            skArc(sketch, "E65.MirrorCS", {"start": v(39.5, -60.5) * mm, "mid": v(37.6, -65.1) * mm, "end": v(33, -67) * mm});
            skCircle(sketch, "E66.MirrorC", {"center": v(33, -60.5) * mm, "radius": 1.63 * mm});
            skArc(sketch, "E67.MirrorCS", {"start": v(27.83, -51.44) * mm, "mid": v(24.31, -48.54) * mm, "end": v(19.88, -47.5) * mm});
            skLineSegment(sketch, "E68", {"start": v(-19.88, -47.5) * mm, "end": v(19.88, -47.5) * mm});
            skLineSegment(sketch, "E69", {"start": v(-33, -67) * mm, "end": v(33, -67) * mm});
            skSolve(sketch);
        }
        {
            var Q0;
            Q0 = qSketchRegion(id + "F39", true);
            var Q1;
            Q1=makeQuery(id+"F26.boolean.opBoolean","MERGE",FACE,{"derivedFrom":[makeQuery(id+"F11.boolean.opBoolean","COPY",FACE,{"derivedFrom":makeQuery(id+"F11.opExtrude","SWEPT_FACE",FACE,{"disambiguationData":[OSD([sQuery(id+"F10.wireOp",EDGE,"E20.rect.bottom")])]})}),makeQuery(id+"F26.opExtrude","SWEPT_FACE",FACE,{"disambiguationData":[OSD([sQuery(id+"F25.wireOp",EDGE,"E40.bottom")])]})]});
            extrude(context, id + "F40", {"entities" : qUnion([Q0]), "operationType" : NewBodyOperationType.ADD, "endBound" : BoundingType.UP_TO_SURFACE, "oppositeDirection" : true, "endBoundEntityFace" : qUnion([Q1]), "depth" : 25 * mm});
        }
        {
            var Q0;
            Q0=makeQuery(id+"F40.boolean.opBoolean","MERGE",FACE,{"derivedFrom":[makeQuery(id+"F21.boolean.opBoolean","MERGE",FACE,{"derivedFrom":[makeQuery(id+"F19.opExtrude","CAP_FACE",FACE,{"disambiguationData":[OSD([sQuery(id+"F18.wireOp",EDGE,"E31.bottom"),sQuery(id+"F18.wireOp",EDGE,"E31.top"),sQuery(id+"F18.wireOp",EDGE,"E31.left"),sQuery(id+"F18.wireOp",EDGE,"E31.right")])],"isStart":false}),makeQuery(id+"F21.opExtrude","CAP_FACE",FACE,{"disambiguationData":[OSD([sQuery(id+"F20.wireOp",EDGE,"E32")])],"isStart":true}),makeQuery(id+"F21.opExtrude","CAP_FACE",FACE,{"disambiguationData":[OSD([sQuery(id+"F20.wireOp",EDGE,"E33")])],"isStart":true}),makeQuery(id+"F21.opExtrude","CAP_FACE",FACE,{"disambiguationData":[OSD([sQuery(id+"F20.wireOp",EDGE,"E34")])],"isStart":true}),makeQuery(id+"F21.opExtrude","CAP_FACE",FACE,{"disambiguationData":[OSD([sQuery(id+"F20.wireOp",EDGE,"E35")])],"isStart":true})]}),makeQuery(id+"F40.opExtrude","CAP_FACE",FACE,{"disambiguationData":[OSD([sQuery(id+"F39.wireOp",EDGE,"E56"),sQuery(id+"F39.wireOp",EDGE,"E57.0"),sQuery(id+"F39.wireOp",EDGE,"E57.1"),sQuery(id+"F39.wireOp",EDGE,"E58"),sQuery(id+"F39.wireOp",EDGE,"E59"),sQuery(id+"F39.wireOp",EDGE,"E62.MirrorCS"),sQuery(id+"F39.wireOp",EDGE,"E64.MirrorCS"),sQuery(id+"F39.wireOp",EDGE,"E65.MirrorCS"),sQuery(id+"F39.wireOp",EDGE,"E66.MirrorC"),sQuery(id+"F39.wireOp",EDGE,"E67.MirrorCS"),sQuery(id+"F39.wireOp",EDGE,"E68"),sQuery(id+"F39.wireOp",EDGE,"E69")])],"isStart":true})]});
            var sketch = newSketch(context, id + "F41", { "sketchPlane" : qUnion([Q0])});
            skCircle(sketch, "E70", {"center": v(-37.6, -65.1) * mm, "radius": 5 * mm});
            skCircle(sketch, "E71", {"center": v(-37.6, 52.1) * mm, "radius": 5 * mm});
            skCircle(sketch, "E72", {"center": v(37.6, 52.1) * mm, "radius": 5 * mm});
            skCircle(sketch, "E73", {"center": v(37.6, -65.1) * mm, "radius": 5 * mm});
            skSolve(sketch);
        }
        {
            var Q0;
            Q0 = qSketchRegion(id + "F41", true);
            extrude(context, id + "F42", {"entities" : qUnion([Q0]), "operationType" : NewBodyOperationType.ADD, "oppositeDirection" : true, "depth" : 0.5 * mm});
        }
    });
